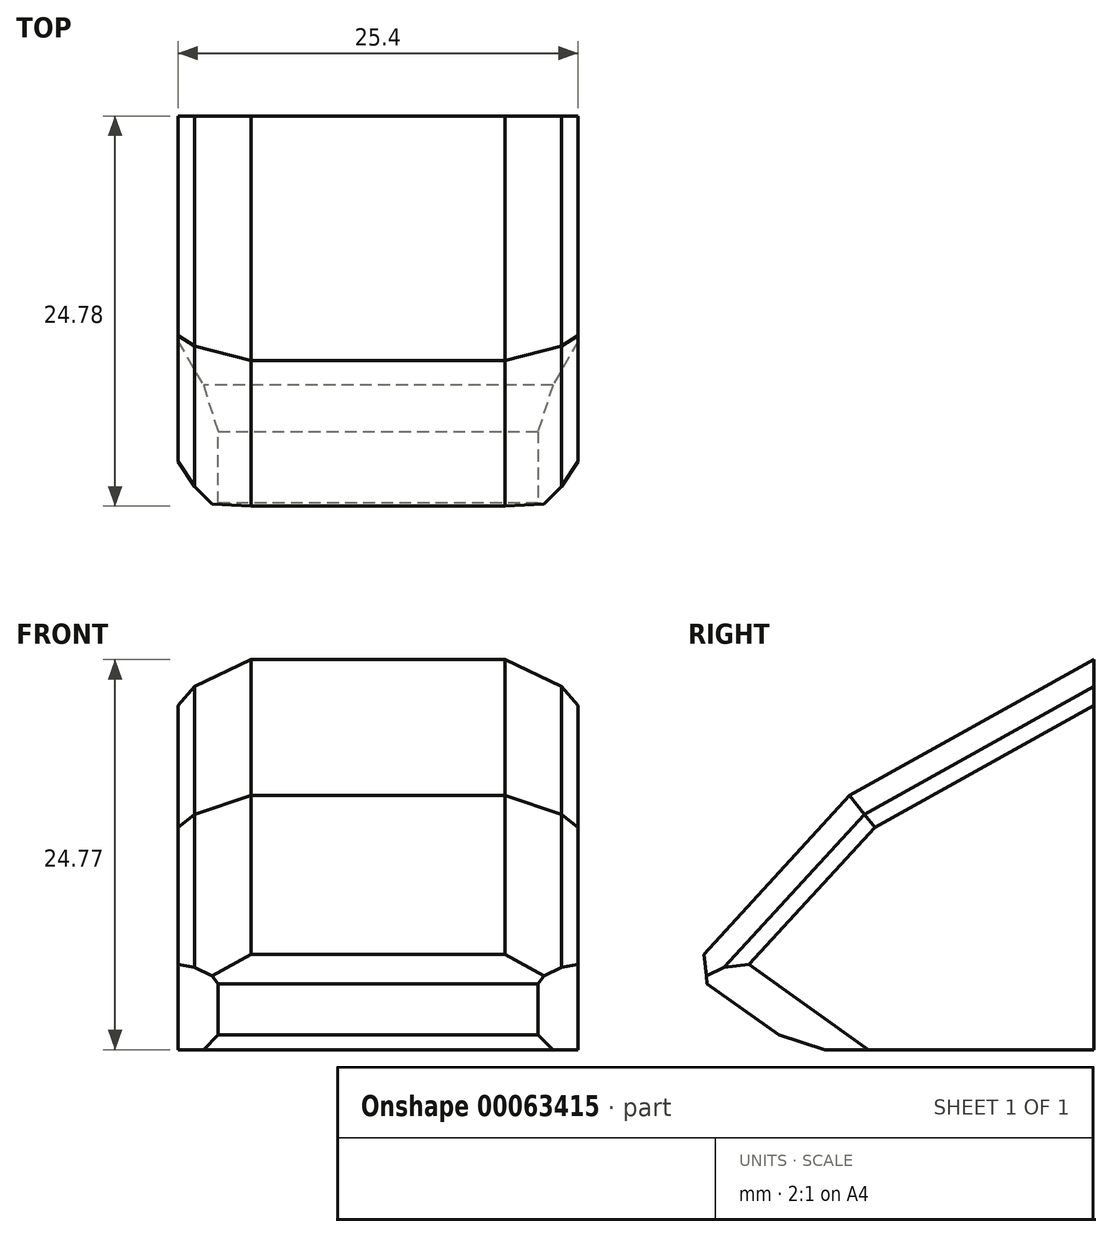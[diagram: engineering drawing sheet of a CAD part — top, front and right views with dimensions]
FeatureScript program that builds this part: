
annotation { "Feature Type Name" : "Feature", "Feature Type Description" : "" }
export const myFeature = defineFeature(function(context is Context, id is Id, definition is map)
    precondition{}
    {
        {
            var Q0;
            Q0=qCreatedBy(makeId("Right.planeOp"),FACE);
            cPlane(context, id + "F0", {"entities" : qUnion([Q0]), "cplaneType" : CPlaneType.OFFSET, "offset" : 152.4 * mm, "width" : 152.4 * mm, "height" : 152.4 * mm});
        }
        {
            var Q0;
            Q0=qCreatedBy(id+"F0.planeOp",FACE);
            var sketch = newSketch(context, id + "F1", { "sketchPlane" : qUnion([Q0])});
            skLineSegment(sketch, "E0", {"start": v(12, 15.6) * mm, "end": v(-3.53, 6.96) * mm});
            skLineSegment(sketch, "E1", {"start": v(-3.53, 6.96) * mm, "end": v(-13.76, -4.18) * mm});
            skLineSegment(sketch, "E2", {"start": v(-13.76, -4.18) * mm, "end": v(-6.7, -9.18) * mm});
            skLineSegment(sketch, "E3", {"start": v(-6.7, -9.18) * mm, "end": v(12, -9.18) * mm});
            skLineSegment(sketch, "E4", {"start": v(12, -9.18) * mm, "end": v(12, 15.6) * mm});
            skSolve(sketch);
        }
        {
            var Q0;
            Q0=makeQuery(id+"F1.imprint","IMPRINT",FACE,{"disambiguationData":[TD([[makeQuery(id+"F1.imprint","IMPRINT",EDGE,{"derivedFrom":sQuery(id+"F1.wireOp",EDGE,"E0")}),1.0]])]});
            extrude(context, id + "F2", {"entities" : qUnion([Q0]), "depth" : 25.4 * mm});
        }
        {
            var Q0;
            Q0=makeQuery(id+"F2.opExtrude","SWEPT_EDGE",EDGE,{"disambiguationData":[OSD([sQuery(id+"F1.wireOp",EDGE,"E1"),sQuery(id+"F1.wireOp",EDGE,"E2")])]});
            chamfer(context, id + "F3", {"entities" : qUnion([Q0]), "width" : 1.27 * mm, "tangentPropagation" : true});
        }
        {
            var Q0;
            Q0=makeQuery(id+"F2.opExtrude","CAP_EDGE",EDGE,{"disambiguationData":[OSD([sQuery(id+"F1.wireOp",EDGE,"E1")])],"isStart":false});
            var Q1;
            Q1=makeQuery(id+"F2.opExtrude","CAP_EDGE",EDGE,{"disambiguationData":[OSD([sQuery(id+"F1.wireOp",EDGE,"E1")])],"isStart":true});
            var Q2;
            Q2=makeQuery(id+"F2.opExtrude","CAP_EDGE",EDGE,{"disambiguationData":[OSD([sQuery(id+"F1.wireOp",EDGE,"E0")])],"isStart":false});
            var Q3;
            Q3=makeQuery(id+"F2.opExtrude","CAP_EDGE",EDGE,{"disambiguationData":[OSD([sQuery(id+"F1.wireOp",EDGE,"E2")])],"isStart":false});
            var Q4;
            Q4=makeQuery(id+"F2.opExtrude","CAP_EDGE",EDGE,{"disambiguationData":[OSD([sQuery(id+"F1.wireOp",EDGE,"E2")])],"isStart":true});
            var Q5;
            Q5=makeQuery(id+"F2.opExtrude","CAP_EDGE",EDGE,{"disambiguationData":[OSD([sQuery(id+"F1.wireOp",EDGE,"E0")])],"isStart":true});
            chamfer(context, id + "F4", {"entities" : qUnion([Q0, Q1, Q2, Q3, Q4, Q5]), "width" : 2.54 * mm, "tangentPropagation" : true});
        }
        {
            var Q0;
            {var subQ0=sQuery(id+"F1.wireOp",EDGE,"E1");Q0=makeQuery(id+"F4.opChamfer","BLEND_EDGE",EDGE,{"blendedFrom":[makeQuery(id+"F2.opExtrude","CAP_EDGE",EDGE,{"disambiguationData":[OSD([subQ0])],"isStart":true}),makeQuery(id+"F2.opExtrude","SWEPT_FACE",FACE,{"disambiguationData":[OSD([subQ0])]})],"blendedInto":[makeQuery(id+"F2.opExtrude","SWEPT_FACE",FACE,{"disambiguationData":[OSD([subQ0])]})]});}
            var Q1;
            {var subQ0=sQuery(id+"F1.wireOp",EDGE,"E0");Q1=makeQuery(id+"F4.opChamfer","BLEND_EDGE",EDGE,{"blendedFrom":[makeQuery(id+"F2.opExtrude","CAP_EDGE",EDGE,{"disambiguationData":[OSD([subQ0])],"isStart":true}),makeQuery(id+"F2.opExtrude","SWEPT_FACE",FACE,{"disambiguationData":[OSD([subQ0])]})],"blendedInto":[makeQuery(id+"F2.opExtrude","SWEPT_FACE",FACE,{"disambiguationData":[OSD([subQ0])]})]});}
            var Q2;
            {var subQ0=sQuery(id+"F1.wireOp",EDGE,"E0");Q2=makeQuery(id+"F4.opChamfer","BLEND_EDGE",EDGE,{"blendedFrom":[makeQuery(id+"F2.opExtrude","CAP_EDGE",EDGE,{"disambiguationData":[OSD([subQ0])],"isStart":false}),makeQuery(id+"F2.opExtrude","SWEPT_FACE",FACE,{"disambiguationData":[OSD([subQ0])]})],"blendedInto":[makeQuery(id+"F2.opExtrude","SWEPT_FACE",FACE,{"disambiguationData":[OSD([subQ0])]})]});}
            var Q3;
            {var subQ0=sQuery(id+"F1.wireOp",EDGE,"E1");Q3=makeQuery(id+"F4.opChamfer","BLEND_EDGE",EDGE,{"blendedFrom":[makeQuery(id+"F2.opExtrude","CAP_EDGE",EDGE,{"disambiguationData":[OSD([subQ0])],"isStart":false}),makeQuery(id+"F2.opExtrude","SWEPT_FACE",FACE,{"disambiguationData":[OSD([subQ0])]})],"blendedInto":[makeQuery(id+"F2.opExtrude","SWEPT_FACE",FACE,{"disambiguationData":[OSD([subQ0])]})]});}
            var Q4;
            Q4=makeQuery(id+"F2.opExtrude","SWEPT_EDGE",EDGE,{"disambiguationData":[OSD([sQuery(id+"F1.wireOp",EDGE,"E2"),sQuery(id+"F1.wireOp",EDGE,"E3")])]});
            chamfer(context, id + "F5", {"entities" : qUnion([Q0, Q1, Q2, Q3, Q4]), "width" : 5.08 * mm, "tangentPropagation" : true});
        }
    });
